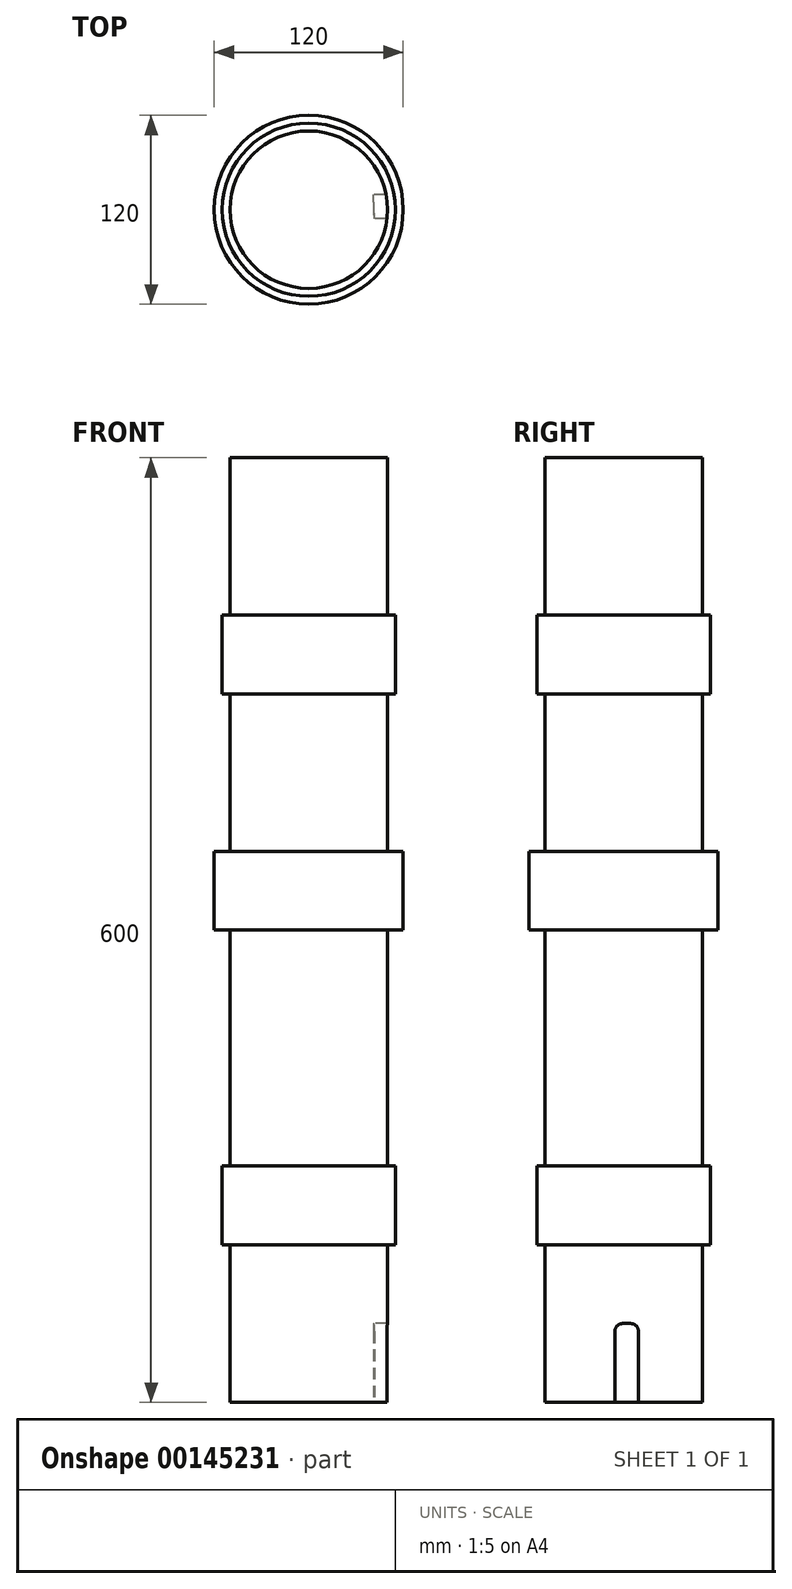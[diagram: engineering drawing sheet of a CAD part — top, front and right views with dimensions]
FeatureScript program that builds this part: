
annotation { "Feature Type Name" : "Feature", "Feature Type Description" : "" }
export const myFeature = defineFeature(function(context is Context, id is Id, definition is map)
    precondition{}
    {
        {
            var Q0;
            Q0=qCreatedBy(makeId("Right.planeOp"),FACE);
            var sketch = newSketch(context, id + "F0", { "sketchPlane" : qUnion([Q0])});
            skLineSegment(sketch, "E0", {"start": v(0, -300) * mm, "end": v(0, 300) * mm, "construction": true});
            skLineSegment(sketch, "E1", {"start": v(0, -300) * mm, "end": v(-50, -300) * mm});
            skLineSegment(sketch, "E2", {"start": v(-50, -300) * mm, "end": v(-50, -200) * mm});
            skLineSegment(sketch, "E3", {"start": v(-50, -200) * mm, "end": v(-55, -200) * mm});
            skLineSegment(sketch, "E4", {"start": v(-55, -200) * mm, "end": v(-55, -150) * mm});
            skLineSegment(sketch, "E5", {"start": v(-55, -150) * mm, "end": v(-50, -150) * mm});
            skLineSegment(sketch, "E6", {"start": v(-50, -150) * mm, "end": v(-50, -50) * mm});
            skLineSegment(sketch, "E7", {"start": v(-50, -50) * mm, "end": v(-60, -50) * mm});
            skLineSegment(sketch, "E8", {"start": v(-60, -50) * mm, "end": v(-60, 50) * mm});
            skLineSegment(sketch, "E9", {"start": v(-60, 50) * mm, "end": v(-50, 50) * mm});
            skLineSegment(sketch, "E10", {"start": v(-50, 50) * mm, "end": v(-50, 150) * mm});
            skLineSegment(sketch, "E11", {"start": v(-50, 150) * mm, "end": v(-55, 150) * mm});
            skLineSegment(sketch, "E12", {"start": v(-55, 150) * mm, "end": v(-55, 200) * mm});
            skLineSegment(sketch, "E13", {"start": v(-55, 200) * mm, "end": v(-50, 200) * mm});
            skLineSegment(sketch, "E14", {"start": v(-50, 200) * mm, "end": v(-50, 300) * mm});
            skLineSegment(sketch, "E15", {"start": v(-50, 300) * mm, "end": v(0, 300) * mm});
            skLineSegment(sketch, "E16", {"start": v(0, 300) * mm, "end": v(0, -300) * mm});
            skSolve(sketch);
        }
        {
            var Q0;
            Q0 = qSketchRegion(id + "F0", true);
            var Q1;
            Q1=sQuery(id+"F0.wireOp",EDGE,"E16");
            revolve(context, id + "F1", {"entities" : qUnion([Q0]), "axis" : qUnion([Q1]), "revolveType" : RevolveType.FULL});
        }
        {
            var Q0;
            Q0=makeQuery(id+"F1.opRevolve","SWEPT_FACE",FACE,{"disambiguationData":[OSD([sQuery(id+"F0.wireOp",EDGE,"E1")])]});
            var sketch = newSketch(context, id + "F2", { "sketchPlane" : qUnion([Q0])});
            skLineSegment(sketch, "E17", {"start": v(-31.7, 0) * mm, "end": v(88.26, 0) * mm, "construction": true});
            skArc(sketch, "E18.0", {"start": v(49.1, -9.43) * mm, "mid": v(49.96, -1.96) * mm, "end": v(49.7, 5.56) * mm});
            skLineSegment(sketch, "E19.bottom", {"start": v(49.7, 5.56) * mm, "end": v(41.7, 5.56) * mm});
            skLineSegment(sketch, "E19.top", {"start": v(49.1, -9.43) * mm, "end": v(41.1, -9.43) * mm});
            skLineSegment(sketch, "E19.right", {"start": v(41.7, 5.56) * mm, "end": v(41.1, -9.43) * mm});
            skPoint(sketch, "E19.middle", {"position": v(50, 0) * mm});
            skSolve(sketch);
        }
        {
            var Q0;
            Q0=makeQuery(id+"F2.imprint","IMPRINT",FACE,{"disambiguationData":[TD([[makeQuery(id+"F2.imprint","IMPRINT",EDGE,{"derivedFrom":sQuery(id+"F2.wireOp",EDGE,"E18.0")}),-1.0]])]});
            var Q1;
            Q1=makeQuery(id+"F1.opRevolve","SWEPT_FACE",FACE,{"disambiguationData":[OSD([sQuery(id+"F0.wireOp",EDGE,"E7")])]});
            extrude(context, id + "F3", {"entities" : qUnion([Q0, Q1]), "operationType" : NewBodyOperationType.REMOVE, "oppositeDirection" : true, "depth" : 50 * mm});
        }
        {
            var Q0;
            Q0=makeQuery(id+"F3.boolean.opBoolean","COPY",EDGE,{"derivedFrom":makeQuery(id+"F3.opExtrude","CAP_EDGE",EDGE,{"disambiguationData":[OSD([sQuery(id+"F2.wireOp",EDGE,"E19.top")])],"isStart":false})});
            var Q1;
            Q1=makeQuery(id+"F3.boolean.opBoolean","COPY",EDGE,{"derivedFrom":makeQuery(id+"F3.opExtrude","CAP_EDGE",EDGE,{"disambiguationData":[OSD([sQuery(id+"F2.wireOp",EDGE,"E19.bottom")])],"isStart":false})});
            fillet(context, id + "F4", {"entities" : qUnion([Q0, Q1]), "radius" : 5 * mm, "tangentPropagation" : true, "allowEdgeOverflow" : false});
        }
    });
